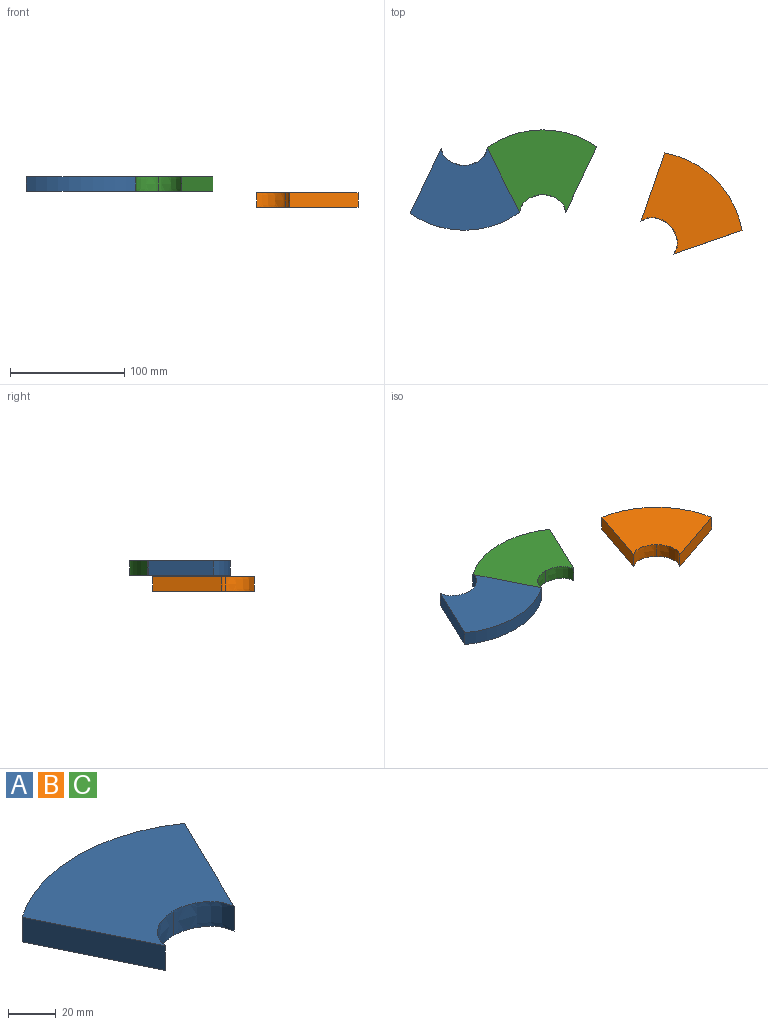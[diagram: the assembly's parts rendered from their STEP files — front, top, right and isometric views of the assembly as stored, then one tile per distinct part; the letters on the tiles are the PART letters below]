
ASSEMBLY  parts=3 mates=1
PART A: 7 faces, bbox 96.1x72.3x12.7 mm
  f0: plane 57.1x27.79mm, normal (0.9,-0.44,0), area 806.4mm2, adj f1,f4,f5,f6
  f1: cylinder r=83.65mm len=96.11mm, axis (0,0,-1), area 1300.3mm2, adj f0,f2,f5,f6
  f2: plane 57.1x27.79mm, normal (-0.9,-0.44,0), area 806.4mm2, adj f1,f3,f5,f6
  f3: extruded ~20.27x15.47mm, area 354.7mm2, adj f2,f4,f5,f6
  f4: extruded ~20.27x15.47mm, area 354.7mm2, adj f0,f3,f5,f6
  f5: plane 96.11x72.28mm, normal (0,0,1), area 4410mm2, adj f0,f1,f2,f3,f4
  f6: plane 96.11x72.28mm, normal (0,0,-1), area 4410mm2, adj f0,f1,f2,f3,f4
PART B: same geometry as A
PART C: same geometry as A
PLACE A rot(axis=(0,0,-1),179.5deg) t=(-161.64,77.13,7.63)mm
PLACE B rot(axis=(0,0,-1),45deg) t=(7.67,-1.71,-6.35)mm
PLACE C rot(axis=(0,0,1),0.5deg) t=(-92.83,20.63,7.63)mm
MATE fastened C.f2 <-> A.f2  axis (-0.9,-0.45,0) through (-127.23,48.88,13.98)mm
